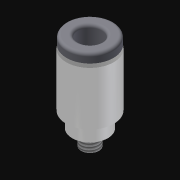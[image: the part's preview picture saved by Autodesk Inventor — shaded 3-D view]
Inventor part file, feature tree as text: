
AUTODESK INVENTOR PART (.ipt)
format: ipt  version: 2021 (Build 250183000, 183)  size: 161,280 bytes
history: native  units: in
note: dims shown in document units (in); Inventor stores cm internally (conversion verified against a paired STEP export)
features: hole x1, imported_body x1, thread x1
ambient origin geometry x8: Origin, YZ Plane, XZ Plane, XY Plane, X Axis, Y Axis, Z Axis, Center Point
bodies: Body1 (feature_tree)
feature tree (3):
  hole  "Hole"  [1 undecoded]
  imported_body  "Base1"
  thread  "Thread1"  [1 undecoded]
note: 2 required parameter values undecoded (feature->parameter linkage not recoverable at this tier; creation-order binding heuristic only, values carry confidence <= 0.55)
